# Revit family: 71_98_2003_NESTED
name_source: partatom
category: Communication Devices
revit_build: Autodesk Revit 2015 (Build: 20140606_1530(x64)
units: mm (PartAtom-declared; Revit-internal decimal feet)

## types (3) — shared parameters
Basisplaat = Basisplaat
Breedte = 155 mm  [stored 0.50853 ft]
Card reader = ISO 14443 MIFARE Card
Reader
DESfire support
DESfire support
Connector = Snap and lock mini DIN
power plug
Consumption = 15 W
Continuous output current = 2 A (per port)
Default Elevation = 1219 mm
Dynamic range = 97 dB / 102 dBA
Frequency response = 200-20,000 Hz (-3 dB)
Jack = Jack
Kabel = Kabel
Knoppen = Inox
Lengte = 330 mm  [stored 1.08268 ft]
Load impedance = 4 Ω
Manufacturer = Televic Conference
Maximum output power = 1.3 W (Zload 8 Ohm)
Model = uniCOS T/MM10
Onderplaat = Inox
Product ID = 71.98.2003
Scherm = Jack
Schroef = Basisplaat
Speaker = Jack
THD @ nominal level = < 0.1% (@ -20 dBFS)
Type Comments = uniCOS 10” Tabletop Multimedia Unit
URL = http://www.televic-conference.com
Voltage = 48 V
zero-valued in all types: Weight

## per-type parameters (varying)
| type | Flexible microphone - 71.03.3540 | Microphone - 71.03.3140 |
| Type 71.98.2003 - no microphone | No | No |
| Type 71.98.2003 - microphone | No | Yes |
| Type 71.98.2003 - flexible microphone | Yes | No |

note: [stored X ft] marks values corroborated as IEEE doubles in the binary element streams (Revit-internal decimal feet)

## geometry (parser evidence)
native form markers: Sweep x26
no freeform markers — native parametric forms only
